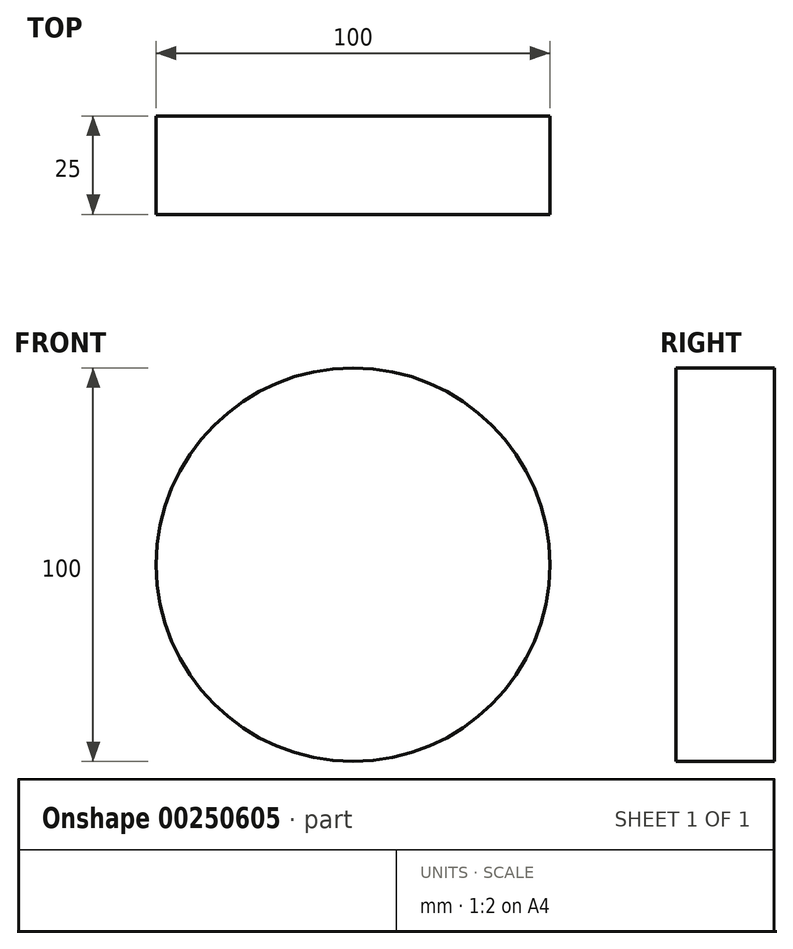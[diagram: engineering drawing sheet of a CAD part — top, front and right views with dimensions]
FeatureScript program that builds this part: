
annotation { "Feature Type Name" : "Feature", "Feature Type Description" : "" }
export const myFeature = defineFeature(function(context is Context, id is Id, definition is map)
    precondition{}
    {
        {
            var Q0;
            Q0=qCreatedBy(makeId("Front.planeOp"),FACE);
            var sketch = newSketch(context, id + "F0", { "sketchPlane" : qUnion([Q0])});
            skCircle(sketch, "E0", {"center": v(0, 0) * mm, "radius": 50 * mm});
            skSolve(sketch);
        }
        {
            var Q0;
            Q0=makeQuery(id+"F0.imprint","IMPRINT",FACE,{"disambiguationData":[TD([[makeQuery(id+"F0.imprint","IMPRINT",EDGE,{"derivedFrom":sQuery(id+"F0.wireOp",EDGE,"E0")}),1.0]])]});
            extrude(context, id + "F1", {"entities" : qUnion([Q0]), "depth" : 25 * mm});
        }
    });
